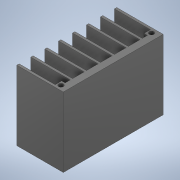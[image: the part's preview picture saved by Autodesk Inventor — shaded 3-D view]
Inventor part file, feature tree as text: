
AUTODESK INVENTOR PART (.ipt)
format: ipt  version: 2020 (Build 240168000, 168)  size: 163,328 bytes
history: native  units: mm
features: extrude x2, sketch x2, other x1
ambient origin geometry x8: Origin, YZ Plane, XZ Plane, XY Plane, X Axis, Y Axis, Z Axis, Center Point
bodies: Body1 (feature_tree)
feature tree (5):
  other  "Твердое тело1"
  extrude  "Выдавливание1"  Depth=43.0mm
  extrude  "Выдавливание2"  Depth=3.0mm
  sketch  "Эскиз1"
  sketch  "Эскиз3"
